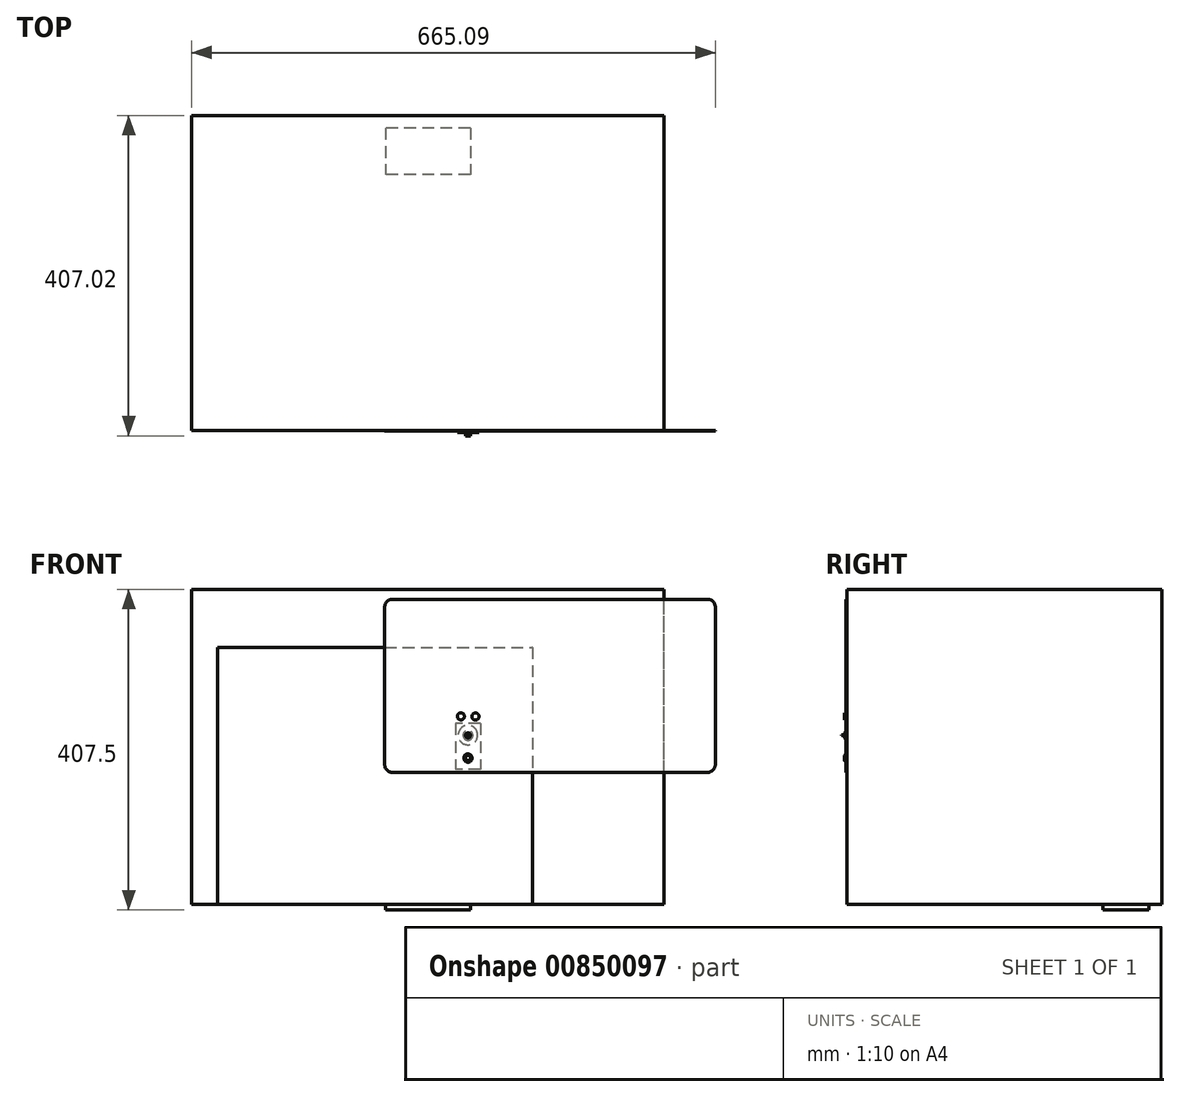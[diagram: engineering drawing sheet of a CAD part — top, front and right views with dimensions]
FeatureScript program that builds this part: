
annotation { "Feature Type Name" : "Feature", "Feature Type Description" : "" }
export const myFeature = defineFeature(function(context is Context, id is Id, definition is map)
    precondition{}
    {
        {
            var Q0;
            Q0=qCreatedBy(makeId("Front.planeOp"),FACE);
            var sketch = newSketch(context, id + "F0", { "sketchPlane" : qUnion([Q0])});
            skLineSegment(sketch, "E0.bottom", {"start": v(300, -200) * mm, "end": v(-300, -200) * mm});
            skLineSegment(sketch, "E0.top", {"start": v(300, 200) * mm, "end": v(-300, 200) * mm});
            skLineSegment(sketch, "E0.left", {"start": v(300, -200) * mm, "end": v(300, 200) * mm});
            skLineSegment(sketch, "E0.right", {"start": v(-300, -200) * mm, "end": v(-300, 200) * mm});
            skPoint(sketch, "E0.middle", {"position": v(0, 0) * mm});
            skSolve(sketch);
        }
        {
            var Q0;
            Q0 = qSketchRegion(id + "F0", true);
            extrude(context, id + "F1", {"entities" : qUnion([Q0]), "depth" : 400 * mm, "offsetDistance" : 25 * mm});
        }
        {
            var Q0;
            Q0=makeQuery(id+"F1.opExtrude","SWEPT_FACE",FACE,{"disambiguationData":[OSD([sQuery(id+"F0.wireOp",EDGE,"E0.bottom")])]});
            var sketch = newSketch(context, id + "F2", { "sketchPlane" : qUnion([Q0])});
            skLineSegment(sketch, "E1.bottom", {"start": v(53.88, 15.98) * mm, "end": v(-53.88, 15.98) * mm});
            skLineSegment(sketch, "E1.top", {"start": v(53.88, 74.95) * mm, "end": v(-53.88, 74.95) * mm});
            skLineSegment(sketch, "E1.left", {"start": v(53.88, 15.98) * mm, "end": v(53.88, 74.95) * mm});
            skLineSegment(sketch, "E1.right", {"start": v(-53.88, 15.98) * mm, "end": v(-53.88, 74.95) * mm});
            skPoint(sketch, "E1.middle", {"position": v(0, 45.46) * mm});
            skSolve(sketch);
        }
        {
            var Q0;
            Q0 = qSketchRegion(id + "F2", true);
            extrude(context, id + "F3", {"entities" : qUnion([Q0]), "depth" : 7.5 * mm, "offsetDistance" : 25 * mm});
        }
        {
            var Q0;
            Q0=makeQuery(id+"F1.opExtrude","CAP_FACE",FACE,{"disambiguationData":[OSD([sQuery(id+"F0.wireOp",EDGE,"E0.bottom"),sQuery(id+"F0.wireOp",EDGE,"E0.top"),sQuery(id+"F0.wireOp",EDGE,"E0.left"),sQuery(id+"F0.wireOp",EDGE,"E0.right")])],"isStart":false});
            var sketch = newSketch(context, id + "F4", { "sketchPlane" : qUnion([Q0])});
            skLineSegment(sketch, "E2.bottom", {"start": v(-267.22, 126.4) * mm, "end": v(132.78, 126.4) * mm});
            skLineSegment(sketch, "E2.top", {"start": v(-267.22, -223.6) * mm, "end": v(132.78, -223.6) * mm});
            skLineSegment(sketch, "E2.left", {"start": v(-267.22, 126.4) * mm, "end": v(-267.22, -223.6) * mm});
            skLineSegment(sketch, "E2.right", {"start": v(132.78, 126.4) * mm, "end": v(132.78, -223.6) * mm});
            skSolve(sketch);
        }
        {
            var Q0;
            Q0=makeQuery(id+"F4.imprint","IMPRINT",FACE,{"disambiguationData":[TD([[makeQuery(id+"F4.imprint","IMPRINT",EDGE,{"derivedFrom":sQuery(id+"F4.wireOp",EDGE,"E2.bottom")}),-1.0]])]});
            extrude(context, id + "F5", {"entities" : qUnion([Q0]), "depth" : 0.01 * mm, "offsetDistance" : 25 * mm});
        }
        {
            var Q0;
            Q0=makeQuery(id+"F5.opExtrude","CAP_FACE",FACE,{"disambiguationData":[OSD([sQuery(id+"F4.wireOp",EDGE,"E2.bottom"),sQuery(id+"F4.wireOp",EDGE,"E2.top"),sQuery(id+"F4.wireOp",EDGE,"E2.left"),sQuery(id+"F4.wireOp",EDGE,"E2.right")])],"isStart":false});
            fillet(context, id + "F6", {"entities" : qUnion([Q0]), "radius" : 89.33 * mm, "tangentPropagation" : true, "allowEdgeOverflow" : false});
        }
        {
            var Q0;
            Q0=makeQuery(id+"F5.opExtrude","CAP_FACE",FACE,{"disambiguationData":[OSD([sQuery(id+"F4.wireOp",EDGE,"E2.bottom"),sQuery(id+"F4.wireOp",EDGE,"E2.top"),sQuery(id+"F4.wireOp",EDGE,"E2.left"),sQuery(id+"F4.wireOp",EDGE,"E2.right")])],"isStart":false});
            var sketch = newSketch(context, id + "F7", { "sketchPlane" : qUnion([Q0])});
            skLineSegment(sketch, "E3.bottom", {"start": v(-44.91, 187.39) * mm, "end": v(355.09, 187.39) * mm});
            skLineSegment(sketch, "E3.top", {"start": v(-44.91, -32.61) * mm, "end": v(355.09, -32.61) * mm});
            skLineSegment(sketch, "E3.left", {"start": v(-54.91, 177.39) * mm, "end": v(-54.91, -22.61) * mm});
            skLineSegment(sketch, "E3.right", {"start": v(365.09, 177.39) * mm, "end": v(365.09, -22.61) * mm});
            skPoint(sketch, "E4.visualSharp", {"position": v(-54.91, 187.39) * mm});
            skArc(sketch, "E4.filletArc", {"start": v(-44.91, 187.39) * mm, "mid": v(-51.98, 184.46) * mm, "end": v(-54.91, 177.39) * mm});
            skPoint(sketch, "E5.visualSharp", {"position": v(365.09, 187.39) * mm});
            skArc(sketch, "E5.filletArc", {"start": v(365.09, 177.39) * mm, "mid": v(362.16, 184.46) * mm, "end": v(355.09, 187.39) * mm});
            skPoint(sketch, "E6.visualSharp", {"position": v(-54.91, -32.61) * mm});
            skArc(sketch, "E6.filletArc", {"start": v(-54.91, -22.61) * mm, "mid": v(-51.98, -29.69) * mm, "end": v(-44.91, -32.61) * mm});
            skPoint(sketch, "E7.visualSharp", {"position": v(365.09, -32.61) * mm});
            skArc(sketch, "E7.filletArc", {"start": v(355.09, -32.61) * mm, "mid": v(362.16, -29.69) * mm, "end": v(365.09, -22.61) * mm});
            skSolve(sketch);
        }
        {
            var Q0;
            Q0 = qSketchRegion(id + "F7", true);
            extrude(context, id + "F8", {"entities" : qUnion([Q0]), "depth" : 1 * mm, "offsetDistance" : 25 * mm});
        }
        {
            var Q0;
            Q0=makeQuery(id+"F1.opExtrude","CAP_FACE",FACE,{"disambiguationData":[OSD([sQuery(id+"F0.wireOp",EDGE,"E0.bottom"),sQuery(id+"F0.wireOp",EDGE,"E0.top"),sQuery(id+"F0.wireOp",EDGE,"E0.left"),sQuery(id+"F0.wireOp",EDGE,"E0.right")])],"isStart":false});
            var sketch = newSketch(context, id + "F9", { "sketchPlane" : qUnion([Q0])});
            skCircle(sketch, "E8", {"center": v(41.87, 38.54) * mm, "radius": 4.53 * mm});
            skSolve(sketch);
        }
        {
            var Q0;
            Q0 = qSketchRegion(id + "F9", true);
            extrude(context, id + "F10", {"entities" : qUnion([Q0]), "depth" : 3 * mm, "offsetDistance" : 25 * mm});
        }
        {
            var Q0;
            Q0=makeQuery(id+"F1.opExtrude","CAP_FACE",FACE,{"disambiguationData":[OSD([sQuery(id+"F0.wireOp",EDGE,"E0.bottom"),sQuery(id+"F0.wireOp",EDGE,"E0.top"),sQuery(id+"F0.wireOp",EDGE,"E0.left"),sQuery(id+"F0.wireOp",EDGE,"E0.right")])],"isStart":false});
            var sketch = newSketch(context, id + "F11", { "sketchPlane" : qUnion([Q0])});
            skCircle(sketch, "E9", {"center": v(60.4, 38.38) * mm, "radius": 4.53 * mm});
            skSolve(sketch);
        }
        {
            var Q0;
            Q0 = qSketchRegion(id + "F11", true);
            extrude(context, id + "F12", {"entities" : qUnion([Q0]), "depth" : 3 * mm, "offsetDistance" : 25 * mm});
        }
        {
            var Q0;
            Q0=makeQuery(id+"F1.opExtrude","CAP_FACE",FACE,{"disambiguationData":[OSD([sQuery(id+"F0.wireOp",EDGE,"E0.bottom"),sQuery(id+"F0.wireOp",EDGE,"E0.top"),sQuery(id+"F0.wireOp",EDGE,"E0.left"),sQuery(id+"F0.wireOp",EDGE,"E0.right")])],"isStart":false});
            var sketch = newSketch(context, id + "F13", { "sketchPlane" : qUnion([Q0])});
            skLineSegment(sketch, "E10.bottom", {"start": v(66.88, 29.84) * mm, "end": v(34.78, 29.84) * mm});
            skLineSegment(sketch, "E10.top", {"start": v(66.88, -28.85) * mm, "end": v(34.78, -28.85) * mm});
            skLineSegment(sketch, "E10.left", {"start": v(66.88, 29.84) * mm, "end": v(66.88, -28.85) * mm});
            skLineSegment(sketch, "E10.right", {"start": v(34.78, 29.84) * mm, "end": v(34.78, -28.85) * mm});
            skSolve(sketch);
        }
        {
            var Q0;
            Q0 = qSketchRegion(id + "F13", true);
            extrude(context, id + "F14", {"entities" : qUnion([Q0]), "depth" : 0.01 * mm, "offsetDistance" : 25 * mm});
        }
        {
            var Q0;
            Q0=makeQuery(id+"F14.opExtrude","CAP_FACE",FACE,{"disambiguationData":[OSD([sQuery(id+"F13.wireOp",EDGE,"E10.bottom"),sQuery(id+"F13.wireOp",EDGE,"E10.top"),sQuery(id+"F13.wireOp",EDGE,"E10.left"),sQuery(id+"F13.wireOp",EDGE,"E10.right")])],"isStart":false});
            var sketch = newSketch(context, id + "F15", { "sketchPlane" : qUnion([Q0])});
            skLineSegment(sketch, "E11", {"start": v(50.83, 29.84) * mm, "end": v(50.83, -28.85) * mm, "construction": true});
            skLineSegment(sketch, "E12", {"start": v(34.78, 0) * mm, "end": v(66.88, 0) * mm, "construction": true});
            skPoint(sketch, "E12.endSnap0", {"position": v(66.88, 0.5) * mm});
            skLineSegment(sketch, "E13", {"start": v(66.88, 14.78) * mm, "end": v(34.78, 14.78) * mm, "construction": true});
            skLineSegment(sketch, "E14", {"start": v(34.78, -14.38) * mm, "end": v(66.88, -14.38) * mm, "construction": true});
            skCircle(sketch, "E15", {"center": v(50.83, -14.38) * mm, "radius": 12.38 * mm});
            skCircle(sketch, "E16", {"center": v(50.83, 14.78) * mm, "radius": 12.4 * mm});
            skSolve(sketch);
        }
        {
            var Q0;
            Q0=makeQuery(id+"F15.imprint","IMPRINT",FACE,{"disambiguationData":[TD([[makeQuery(id+"F15.imprint","IMPRINT",EDGE,{"derivedFrom":sQuery(id+"F15.wireOp",EDGE,"E16")}),1.0]])]});
            var Q1;
            Q1=makeQuery(id+"F15.imprint","IMPRINT",FACE,{"disambiguationData":[TD([[makeQuery(id+"F15.imprint","IMPRINT",EDGE,{"derivedFrom":sQuery(id+"F15.wireOp",EDGE,"E15")}),1.0]])]});
            extrude(context, id + "F16", {"entities" : qUnion([Q0, Q1]), "depth" : 0.01 * mm, "offsetDistance" : 25 * mm});
        }
        {
            var Q0;
            Q0=makeQuery(id+"F16.opExtrude","CAP_FACE",FACE,{"disambiguationData":[OSD([sQuery(id+"F15.wireOp",EDGE,"E16")])],"isStart":false});
            var sketch = newSketch(context, id + "F17", { "sketchPlane" : qUnion([Q0])});
            skCircle(sketch, "E17", {"center": v(50.92, 14.49) * mm, "radius": 8.17 * mm});
            skPoint(sketch, "E17.first.point", {"position": v(50.73, 22.65) * mm});
            skPoint(sketch, "E17.second.point", {"position": v(42.9, 12.93) * mm});
            skPoint(sketch, "E17.third.point", {"position": v(58.32, 11.03) * mm});
            skSolve(sketch);
        }
        {
            var Q0;
            Q0 = qSketchRegion(id + "F17", true);
            extrude(context, id + "F18", {"entities" : qUnion([Q0]), "depth" : 3 * mm, "offsetDistance" : 25 * mm});
        }
        {
            var Q0;
            Q0=makeQuery(id+"F18.opExtrude","CAP_FACE",FACE,{"disambiguationData":[OSD([sQuery(id+"F17.wireOp",EDGE,"E17")])],"isStart":false});
            chamfer(context, id + "F19", {"entities" : qUnion([Q0]), "width" : 5 * mm, "tangentPropagation" : true});
        }
        {
            var Q0;
            Q0=makeQuery(id+"F16.opExtrude","CAP_FACE",FACE,{"disambiguationData":[OSD([sQuery(id+"F15.wireOp",EDGE,"E15")])],"isStart":false});
            var sketch = newSketch(context, id + "F20", { "sketchPlane" : qUnion([Q0])});
            skCircle(sketch, "E18", {"center": v(50.83, -14.38) * mm, "radius": 8.23 * mm});
            skSolve(sketch);
        }
        {
            var Q0;
            Q0 = qSketchRegion(id + "F20", true);
            extrude(context, id + "F21", {"entities" : qUnion([Q0]), "operationType" : NewBodyOperationType.ADD, "depth" : 3 * mm, "offsetDistance" : 25 * mm});
        }
        {
            var Q0;
            Q0=makeQuery(id+"F21.opExtrude","CAP_FACE",FACE,{"disambiguationData":[OSD([sQuery(id+"F20.wireOp",EDGE,"E18")])],"isStart":false});
            chamfer(context, id + "F22", {"entities" : qUnion([Q0]), "width" : 5 * mm, "tangentPropagation" : true});
        }
        {
            var Q0;
            Q0=makeQuery(id+"F16.opExtrude","CAP_FACE",FACE,{"disambiguationData":[OSD([sQuery(id+"F15.wireOp",EDGE,"E16")])],"isStart":false});
            var sketch = newSketch(context, id + "F23", { "sketchPlane" : qUnion([Q0])});
            skLineSegment(sketch, "E19", {"start": v(51.06, 27.18) * mm, "end": v(51.06, 20.65) * mm});
            skLineSegment(sketch, "E20", {"start": v(51, 8.32) * mm, "end": v(51, 2.37) * mm});
            skLineSegment(sketch, "E21", {"start": v(38.43, 14.26) * mm, "end": v(44.76, 14.26) * mm});
            skLineSegment(sketch, "E22", {"start": v(57.08, 14.26) * mm, "end": v(63.23, 14.26) * mm});
            skLineSegment(sketch, "E23", {"start": v(42.33, 5.74) * mm, "end": v(46.64, 10.04) * mm});
            skLineSegment(sketch, "E24", {"start": v(55.18, 18.95) * mm, "end": v(59.7, 23.46) * mm});
            skLineSegment(sketch, "E25", {"start": v(46.66, 18.95) * mm, "end": v(42.05, 23.55) * mm});
            skLineSegment(sketch, "E26", {"start": v(55.18, 10.03) * mm, "end": v(59.4, 5.8) * mm});
            skLineSegment(sketch, "E27", {"start": v(46.18, 26.28) * mm, "end": v(48.69, 20.24) * mm});
            skLineSegment(sketch, "E28", {"start": v(53.37, 20.15) * mm, "end": v(55.84, 26.13) * mm});
            skLineSegment(sketch, "E29", {"start": v(56.73, 16.55) * mm, "end": v(62.52, 18.95) * mm});
            skLineSegment(sketch, "E30", {"start": v(56.6, 12.07) * mm, "end": v(62.18, 9.76) * mm});
            skLineSegment(sketch, "E31", {"start": v(48.68, 8.74) * mm, "end": v(46.38, 3.2) * mm});
            skLineSegment(sketch, "E32", {"start": v(53.43, 8.85) * mm, "end": v(55.7, 3.36) * mm});
            skLineSegment(sketch, "E33", {"start": v(45.21, 12.16) * mm, "end": v(39.47, 9.78) * mm});
            skLineSegment(sketch, "E34", {"start": v(45.08, 16.48) * mm, "end": v(39.14, 18.95) * mm});
            skSolve(sketch);
        }
        {
            var Q0;
            Q0=sQuery(id+"F23.wireOp",EDGE,"E25");
            var Q1;
            Q1=sQuery(id+"F23.wireOp",EDGE,"E34");
            var Q2;
            Q2=sQuery(id+"F23.wireOp",EDGE,"E21");
            var Q3;
            Q3=sQuery(id+"F23.wireOp",EDGE,"E33");
            var Q4;
            Q4=sQuery(id+"F23.wireOp",EDGE,"E23");
            var Q5;
            Q5=sQuery(id+"F23.wireOp",EDGE,"E31");
            var Q6;
            Q6=sQuery(id+"F23.wireOp",EDGE,"E20");
            var Q7;
            Q7=sQuery(id+"F23.wireOp",EDGE,"E32");
            var Q8;
            Q8=sQuery(id+"F23.wireOp",EDGE,"E26");
            var Q9;
            Q9=sQuery(id+"F23.wireOp",EDGE,"E30");
            var Q10;
            Q10=sQuery(id+"F23.wireOp",EDGE,"E22");
            var Q11;
            Q11=sQuery(id+"F23.wireOp",EDGE,"E29");
            var Q12;
            Q12=sQuery(id+"F23.wireOp",EDGE,"E24");
            var Q13;
            Q13=sQuery(id+"F23.wireOp",EDGE,"E28");
            var Q14;
            Q14=sQuery(id+"F23.wireOp",EDGE,"E19");
            var Q15;
            Q15=sQuery(id+"F23.wireOp",EDGE,"E27");
            extrude(context, id + "F24", {"bodyType" : ToolBodyType.SURFACE, "surfaceEntities" : qUnion([Q0, Q1, Q2, Q3, Q4, Q5, Q6, Q7, Q8, Q9, Q10, Q11, Q12, Q13, Q14, Q15]), "depth" : 0.01 * mm, "offsetDistance" : 25 * mm});
        }
        {
            var Q0;
            Q0=makeQuery(id+"F18.opExtrude","CAP_FACE",FACE,{"disambiguationData":[OSD([sQuery(id+"F17.wireOp",EDGE,"E17")])],"isStart":false});
            var sketch = newSketch(context, id + "F25", { "sketchPlane" : qUnion([Q0])});
            skLineSegment(sketch, "E35.bottom", {"start": v(47.77, 14.8) * mm, "end": v(54.06, 14.8) * mm});
            skLineSegment(sketch, "E35.top", {"start": v(47.77, 14.09) * mm, "end": v(54.06, 14.09) * mm});
            skLineSegment(sketch, "E35.left", {"start": v(47.77, 14.8) * mm, "end": v(47.77, 14.09) * mm});
            skLineSegment(sketch, "E35.right", {"start": v(54.06, 14.8) * mm, "end": v(54.06, 14.09) * mm});
            skSolve(sketch);
        }
        {
            var Q0;
            {var subQ1=sQuery(id+"F25.wireOp",EDGE,"E35.bottom");Q0=makeQuery(id+"F25.imprint","IMPRINT",FACE,{"disambiguationData":[TD([[makeQuery(id+"F25.imprint","IMPRINT",EDGE,{"derivedFrom":subQ1}),-1.0]])]});}
            extrude(context, id + "F26", {"entities" : qUnion([Q0]), "operationType" : NewBodyOperationType.ADD, "depth" : 4 * mm, "offsetDistance" : 25 * mm});
        }
    });
